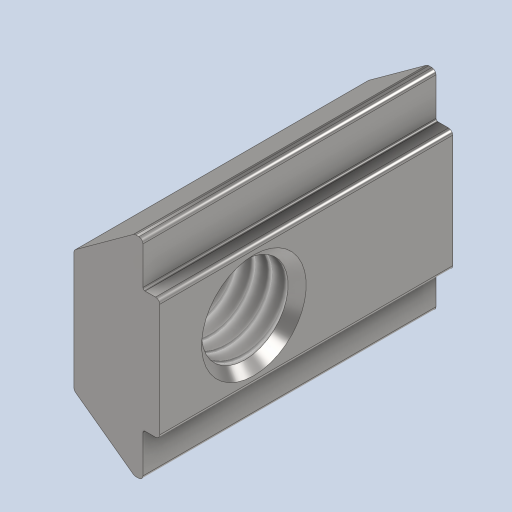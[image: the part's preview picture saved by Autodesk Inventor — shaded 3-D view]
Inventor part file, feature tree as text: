
AUTODESK INVENTOR PART (.ipt)
format: ipt  version: 2023 (Build 270158000, 158)  size: 226,304 bytes
history: native  units: mm
features: other x21, revolve x3, extrude x1, thread x1
ambient origin geometry x8: Origin, YZ Plane, XZ Plane, XY Plane, X Axis, Y Axis, Z Axis, Center Point
bodies: Solid1 (feature_tree)
feature tree (26):
  extrude  "Extrusion1"  Depth=14.0mm TaperAngle=0.0deg
  revolve  "Revolution1"  Angle=360.0deg
  thread  "Thread1"  [1 undecoded]
  revolve  "Revolution2"  Angle=360.0deg
  revolve  "Revolution3"  Angle=360.0deg
  other  "to_blackets_XY"
  other  "to_blackets_YZ"
  other  "to_blackets_ZX"
  other  "to_blackets_X"
  other  "to_blackets_Y"
  other  "to_blackets_Z"
  other  "to_blackets_Center"
  other  "to_bolt_XY"
  other  "to_bolt_YZ"
  other  "to_bolt_ZX"
  other  "to_bolt_X"
  other  "to_bolt_Y"
  other  "to_bolt_Z"
  other  "to_bolt_Center"
  other  "to_frames_XY"
  other  "to_frames_YZ"
  other  "to_frames_ZX"
  other  "to_frames_X"
  other  "to_frames_Y"
  other  "to_frames_Z"
  other  "to_frames_Center"
note: 1 required parameter value undecoded (feature->parameter linkage not recoverable at this tier; creation-order binding heuristic only, values carry confidence <= 0.55)
